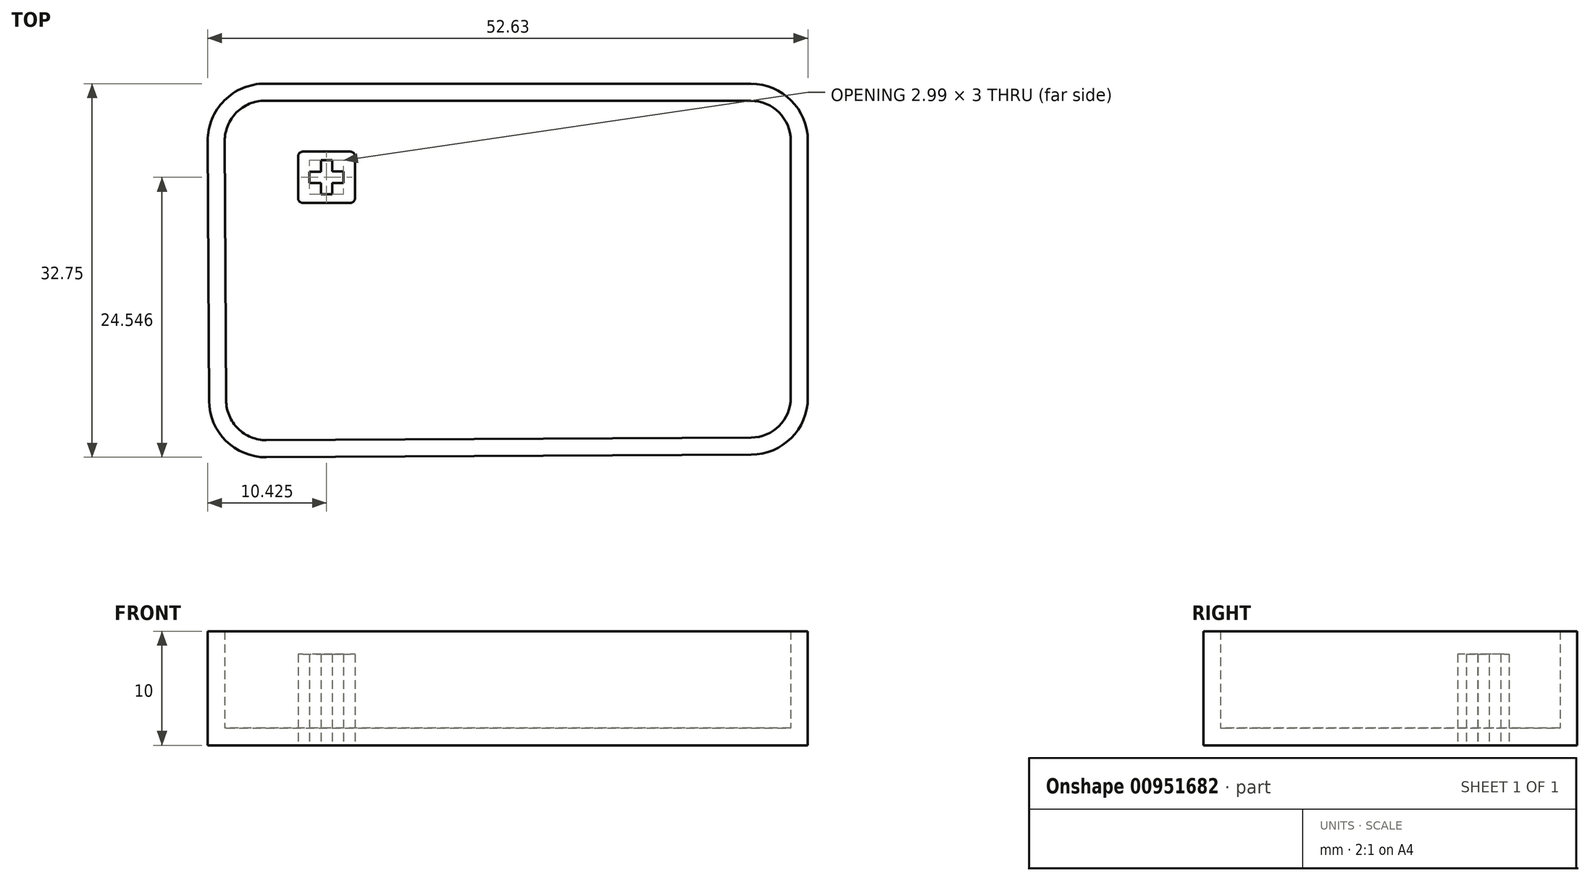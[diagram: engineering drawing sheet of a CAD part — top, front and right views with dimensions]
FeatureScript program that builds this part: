
annotation { "Feature Type Name" : "Feature", "Feature Type Description" : "" }
export const myFeature = defineFeature(function(context is Context, id is Id, definition is map)
    precondition{}
    {
        {
            var Q0;
            Q0=qCreatedBy(makeId("Top.planeOp"),FACE);
            var sketch = newSketch(context, id + "F0", { "sketchPlane" : qUnion([Q0])});
            skLineSegment(sketch, "E0", {"start": v(-1.39, 2.63) * mm, "end": v(-0.39, 2.63) * mm});
            skLineSegment(sketch, "E1", {"start": v(-0.39, 2.63) * mm, "end": v(-0.39, 1.63) * mm});
            skLineSegment(sketch, "E2", {"start": v(-0.39, 1.63) * mm, "end": v(0.6, 1.63) * mm});
            skLineSegment(sketch, "E3", {"start": v(0.6, 1.63) * mm, "end": v(0.6, 0.63) * mm});
            skLineSegment(sketch, "E4", {"start": v(0.6, 0.63) * mm, "end": v(-0.38, 0.63) * mm});
            skLineSegment(sketch, "E5", {"start": v(-0.38, 0.63) * mm, "end": v(-0.38, -0.37) * mm});
            skLineSegment(sketch, "E6", {"start": v(-0.38, -0.37) * mm, "end": v(-1.38, -0.37) * mm});
            skLineSegment(sketch, "E7", {"start": v(-1.38, -0.37) * mm, "end": v(-1.38, 0.62) * mm});
            skLineSegment(sketch, "E8", {"start": v(-1.38, 0.62) * mm, "end": v(-2.38, 0.62) * mm});
            skLineSegment(sketch, "E9", {"start": v(-2.38, 0.62) * mm, "end": v(-2.38, 1.62) * mm});
            skLineSegment(sketch, "E10", {"start": v(-2.38, 1.62) * mm, "end": v(-1.38, 1.62) * mm});
            skLineSegment(sketch, "E11", {"start": v(-1.39, 2.63) * mm, "end": v(-1.38, 1.62) * mm});
            skLineSegment(sketch, "E12.bottom", {"start": v(-2.96, 3.38) * mm, "end": v(1.19, 3.38) * mm});
            skLineSegment(sketch, "E12.top", {"start": v(-2.96, -1.12) * mm, "end": v(1.19, -1.12) * mm});
            skLineSegment(sketch, "E12.left", {"start": v(-3.39, 2.95) * mm, "end": v(-3.39, -0.7) * mm});
            skLineSegment(sketch, "E12.right", {"start": v(1.61, 2.95) * mm, "end": v(1.61, -0.7) * mm});
            skPoint(sketch, "E13.visualSharp", {"position": v(-3.42, 3.3) * mm});
            skArc(sketch, "E13.filletArc", {"start": v(-2.96, 3.38) * mm, "mid": v(-3.26, 3.25) * mm, "end": v(-3.39, 2.95) * mm});
            skPoint(sketch, "E14.visualSharp", {"position": v(1.58, 3.3) * mm});
            skArc(sketch, "E14.filletArc", {"start": v(1.61, 2.95) * mm, "mid": v(1.49, 3.25) * mm, "end": v(1.19, 3.38) * mm});
            skPoint(sketch, "E15.visualSharp", {"position": v(1.58, -1.2) * mm});
            skArc(sketch, "E15.filletArc", {"start": v(1.19, -1.12) * mm, "mid": v(1.49, -1) * mm, "end": v(1.61, -0.7) * mm});
            skPoint(sketch, "E16.visualSharp", {"position": v(-3.42, -1.2) * mm});
            skArc(sketch, "E16.filletArc", {"start": v(-3.39, -0.7) * mm, "mid": v(-3.26, -1) * mm, "end": v(-2.96, -1.12) * mm});
            skSolve(sketch);
        }
        {
            var Q0;
            Q0 = qSketchRegion(id + "F0", true);
            extrude(context, id + "F1", {"entities" : qUnion([Q0]), "depth" : 8 * mm, "offsetDistance" : 25 * mm});
        }
        {
            var Q0;
            Q0=qCreatedBy(makeId("Top.planeOp"),FACE);
            var sketch = newSketch(context, id + "F2", { "sketchPlane" : qUnion([Q0])});
            skLineSegment(sketch, "E17", {"start": v(-6.16, -23.42) * mm, "end": v(36.34, -23.2) * mm});
            skLineSegment(sketch, "E18", {"start": v(41.32, 4.33) * mm, "end": v(41.32, -18.2) * mm});
            skLineSegment(sketch, "E19", {"start": v(36.32, 9.33) * mm, "end": v(-6.3, 9.33) * mm});
            skLineSegment(sketch, "E20", {"start": v(-11.19, -18.44) * mm, "end": v(-11.3, 4.3) * mm});
            skPoint(sketch, "E21.visualSharp", {"position": v(-11.33, 9.33) * mm});
            skArc(sketch, "E21.filletArc", {"start": v(-6.3, 9.33) * mm, "mid": v(-9.85, 7.86) * mm, "end": v(-11.3, 4.3) * mm});
            skPoint(sketch, "E22.visualSharp", {"position": v(41.32, 9.33) * mm});
            skArc(sketch, "E22.filletArc", {"start": v(41.32, 4.33) * mm, "mid": v(39.85, 7.87) * mm, "end": v(36.32, 9.33) * mm});
            skPoint(sketch, "E23.visualSharp", {"position": v(41.32, -23.17) * mm});
            skArc(sketch, "E23.filletArc", {"start": v(36.34, -23.2) * mm, "mid": v(39.86, -21.73) * mm, "end": v(41.32, -18.2) * mm});
            skPoint(sketch, "E24.visualSharp", {"position": v(-11.16, -23.44) * mm});
            skArc(sketch, "E24.filletArc", {"start": v(-11.19, -18.44) * mm, "mid": v(-9.7, -21.97) * mm, "end": v(-6.16, -23.42) * mm});
            skSolve(sketch);
        }
        {
            var Q0;
            Q0=makeQuery(id+"F2.imprint","IMPRINT",FACE,{"disambiguationData":[TD([[makeQuery(id+"F2.imprint","IMPRINT",EDGE,{"derivedFrom":sQuery(id+"F2.wireOp",EDGE,"E17")}),1.0]])]});
            extrude(context, id + "F3", {"entities" : qUnion([Q0]), "depth" : 10 * mm, "offsetDistance" : 25 * mm});
        }
        {
            var Q0;
            Q0=makeQuery(id+"F3.opExtrude","CAP_FACE",FACE,{"disambiguationData":[OSD([sQuery(id+"F2.wireOp",EDGE,"E17"),sQuery(id+"F2.wireOp",EDGE,"E18"),sQuery(id+"F2.wireOp",EDGE,"E19"),sQuery(id+"F2.wireOp",EDGE,"E20"),sQuery(id+"F2.wireOp",EDGE,"E21.filletArc"),sQuery(id+"F2.wireOp",EDGE,"E22.filletArc"),sQuery(id+"F2.wireOp",EDGE,"E23.filletArc"),sQuery(id+"F2.wireOp",EDGE,"E24.filletArc")])],"isStart":false});
            shell(context, id + "F4", {"entities" : qUnion([Q0]), "thickness" : 1.5 * mm});
        }
    });
